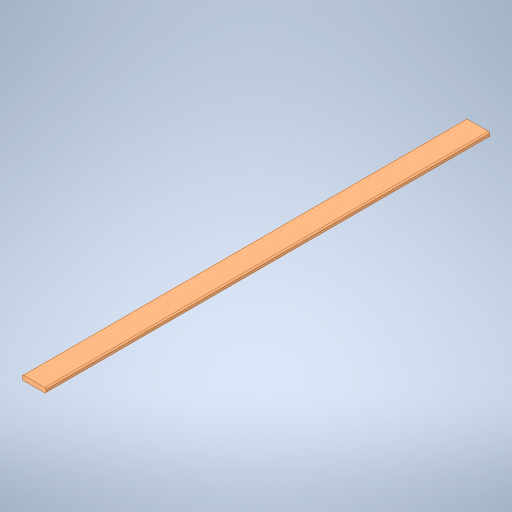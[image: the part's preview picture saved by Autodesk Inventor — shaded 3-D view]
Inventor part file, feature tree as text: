
AUTODESK INVENTOR PART (.ipt)
format: ipt  version: 2024 (Build 280153000, 153)  size: 249,344 bytes
history: native  units: in
note: dims shown in document units (in); Inventor stores cm internally (conversion verified against a paired STEP export)
features: extrude x1, fillet x1
ambient origin geometry x8: Origin, YZ Plane, XZ Plane, XY Plane, X Axis, Y Axis, Z Axis, Center Point
bodies: Solid1 (feature_tree)
feature tree (2):
  extrude  "Extrusion1"  Depth=5.5118in
  fillet  "Fillet1"  Radius=1.1024in
